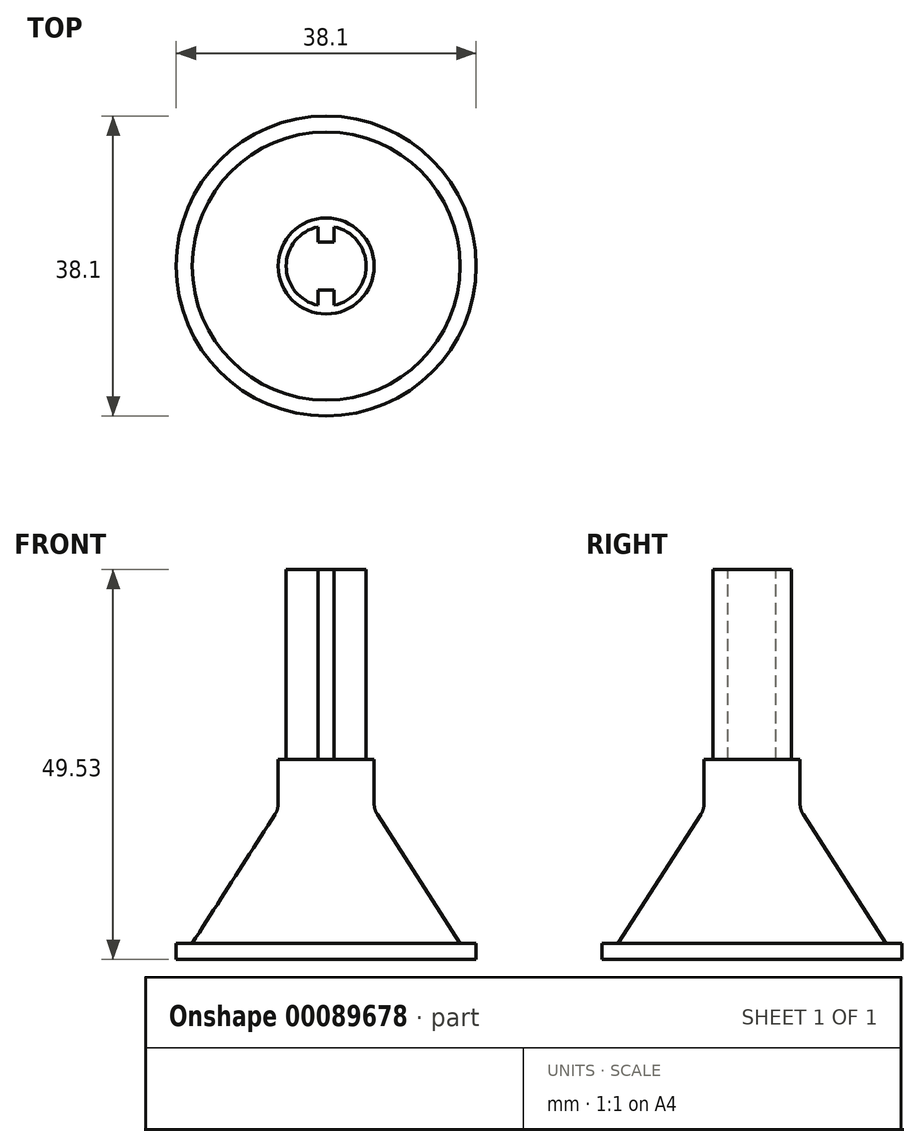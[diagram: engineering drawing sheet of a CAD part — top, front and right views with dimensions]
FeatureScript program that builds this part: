
annotation { "Feature Type Name" : "Feature", "Feature Type Description" : "" }
export const myFeature = defineFeature(function(context is Context, id is Id, definition is map)
    precondition{}
    {
        {
            var Q0;
            Q0=qCreatedBy(makeId("Front.planeOp"),FACE);
            var sketch = newSketch(context, id + "F0", { "sketchPlane" : qUnion([Q0])});
            skLineSegment(sketch, "E0", {"start": v(0, 0) * mm, "end": v(0, 19.05) * mm});
            skLineSegment(sketch, "E1", {"start": v(0, 19.05) * mm, "end": v(6.1, 19.05) * mm});
            skLineSegment(sketch, "E2", {"start": v(19.05, 0) * mm, "end": v(0, 0) * mm});
            skLineSegment(sketch, "E3.left", {"start": v(0, 19.05) * mm, "end": v(0, 19.05) * mm});
            skLineSegment(sketch, "E3.right", {"start": v(6.1, 19.05) * mm, "end": v(6.1, 19.05) * mm});
            skLineSegment(sketch, "E4.top", {"start": v(0, 25.4) * mm, "end": v(6.1, 25.4) * mm});
            skLineSegment(sketch, "E4.left", {"start": v(0, 19.05) * mm, "end": v(0, 25.4) * mm});
            skLineSegment(sketch, "E4.right", {"start": v(6.1, 19.05) * mm, "end": v(6.1, 25.4) * mm});
            skLineSegment(sketch, "E5", {"start": v(19.05, 0) * mm, "end": v(19.05, 2.03) * mm});
            skLineSegment(sketch, "E6", {"start": v(19.05, 2.03) * mm, "end": v(17.02, 2.03) * mm});
            skLineSegment(sketch, "E7", {"start": v(17.02, 2.03) * mm, "end": v(6.1, 19.05) * mm});
            skSolve(sketch);
        }
        {
            var Q0;
            Q0=qSketchRegion(id+"F0",true);
            var Q1;
            Q1=sQuery(id+"F0.wireOp",EDGE,"E0");
            revolve(context, id + "F1", {"entities" : qUnion([Q0]), "axis" : qUnion([Q1]), "revolveType" : RevolveType.FULL});
        }
        {
            var Q0;
            Q0=makeQuery(id+"F1.opRevolve","SWEPT_FACE",FACE,{"disambiguationData":[OSD([sQuery(id+"F0.wireOp",EDGE,"E4.top")])]});
            var sketch = newSketch(context, id + "F2", { "sketchPlane" : qUnion([Q0])});
            skCircle(sketch, "E8", {"center": v(0, 0) * mm, "radius": 5.08 * mm});
            skSolve(sketch);
        }
        {
            var Q0;
            Q0=qSketchRegion(id+"F2",true);
            extrude(context, id + "F3", {"entities" : qUnion([Q0]), "operationType" : NewBodyOperationType.ADD, "depth" : 24.13 * mm});
        }
        {
            var Q0;
            Q0=makeQuery(id+"F1.opRevolve","SWEPT_EDGE",EDGE,{"disambiguationData":[OSD([sQuery(id+"F0.wireOp",EDGE,"99Yukjws-nxL6-M9vy-GY2z-gxU8x74I4FID"),sQuery(id+"F0.wireOp",EDGE,"E1"),sQuery(id+"F0.wireOp",EDGE,"E4.right")])]});
            fillet(context, id + "F4", {"entities" : qUnion([Q0]), "radius" : 2.54 * mm, "tangentPropagation" : true, "allowEdgeOverflow" : false});
        }
        {
            var Q0;
            Q0=makeQuery(id+"F3.opExtrude","CAP_FACE",FACE,{"disambiguationData":[OSD([sQuery(id+"F2.wireOp",EDGE,"E8")])],"isStart":false});
            var sketch = newSketch(context, id + "F5", { "sketchPlane" : qUnion([Q0])});
            skLineSegment(sketch, "E9.bottom", {"start": v(1.02, 5.59) * mm, "end": v(-1.02, 5.59) * mm});
            skLineSegment(sketch, "E9.top", {"start": v(1.02, 3.05) * mm, "end": v(-1.02, 3.05) * mm});
            skLineSegment(sketch, "E9.left", {"start": v(1.02, 5.59) * mm, "end": v(1.02, 3.05) * mm});
            skLineSegment(sketch, "E9.right", {"start": v(-1.02, 5.59) * mm, "end": v(-1.02, 3.05) * mm});
            skPoint(sketch, "E9.middle", {"position": v(0, 4.32) * mm});
            skLineSegment(sketch, "E10.bottom", {"start": v(1.02, -5.59) * mm, "end": v(-1.02, -5.59) * mm});
            skLineSegment(sketch, "E10.top", {"start": v(1.02, -3.05) * mm, "end": v(-1.02, -3.05) * mm});
            skLineSegment(sketch, "E10.left", {"start": v(1.02, -5.59) * mm, "end": v(1.02, -3.05) * mm});
            skLineSegment(sketch, "E10.right", {"start": v(-1.02, -5.59) * mm, "end": v(-1.02, -3.05) * mm});
            skPoint(sketch, "E10.middle", {"position": v(0, -4.32) * mm});
            skSolve(sketch);
        }
        {
            var Q0;
            Q0 = qSketchRegion(id + "F5", true);
            extrude(context, id + "F6", {"entities" : qUnion([Q0]), "operationType" : NewBodyOperationType.REMOVE, "oppositeDirection" : true, "depth" : 24.13 * mm});
        }
    });
